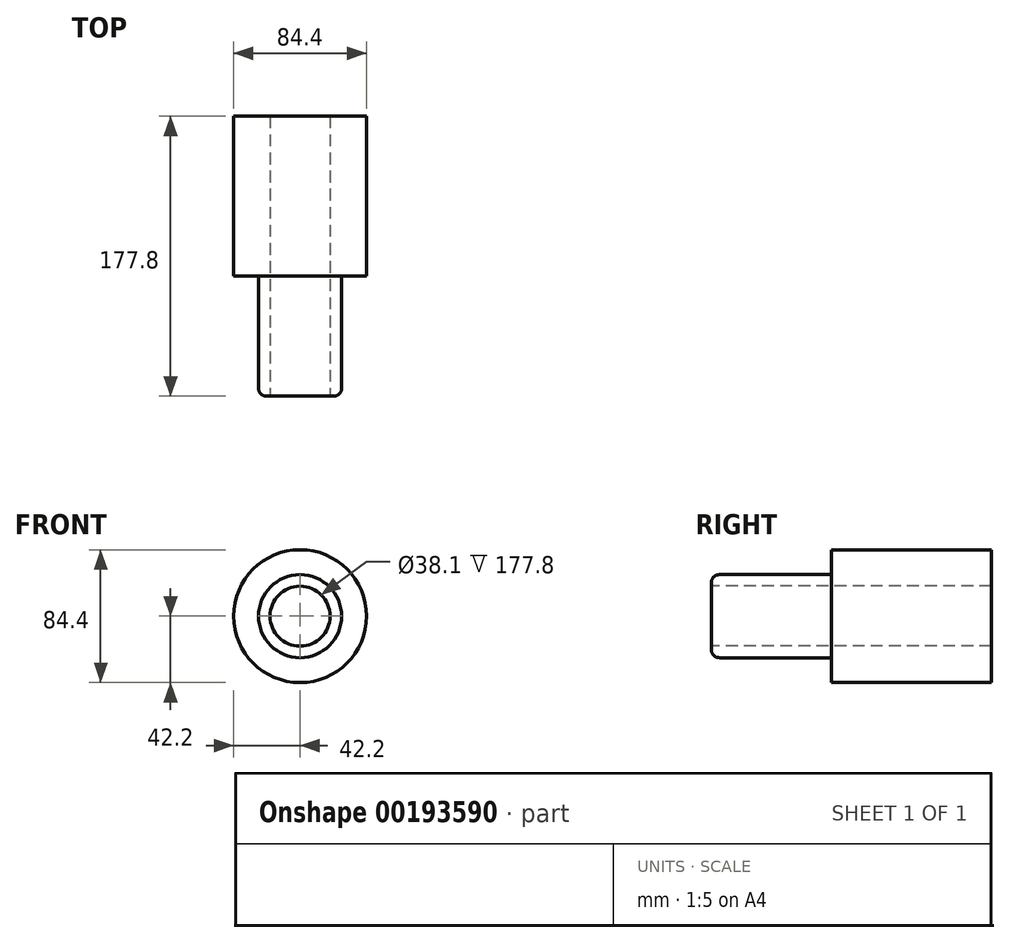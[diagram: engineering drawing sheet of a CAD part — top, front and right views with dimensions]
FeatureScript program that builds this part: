
annotation { "Feature Type Name" : "Feature", "Feature Type Description" : "" }
export const myFeature = defineFeature(function(context is Context, id is Id, definition is map)
    precondition{}
    {
        {
            var Q0;
            Q0=qCreatedBy(makeId("Front.planeOp"),FACE);
            var sketch = newSketch(context, id + "F0", { "sketchPlane" : qUnion([Q0])});
            skCircle(sketch, "E0", {"center": v(0, 0) * mm, "radius": 42.2 * mm});
            skSolve(sketch);
        }
        {
            var Q0;
            Q0=makeQuery(id+"F0.imprint","IMPRINT",FACE,{"disambiguationData":[TD([[makeQuery(id+"F0.imprint","IMPRINT",EDGE,{"derivedFrom":sQuery(id+"F0.wireOp",EDGE,"E0")}),1.0]])]});
            extrude(context, id + "F1", {"entities" : qUnion([Q0]), "depth" : 50.8 * mm});
        }
        {
            var Q0;
            Q0=qCreatedBy(makeId("Front.planeOp"),FACE);
            var sketch = newSketch(context, id + "F2", { "sketchPlane" : qUnion([Q0])});
            skCircle(sketch, "E1", {"center": v(0, 0) * mm, "radius": 26.14 * mm});
            skSolve(sketch);
        }
        {
            var Q0;
            Q0 = qSketchRegion(id + "F2", true);
            extrude(context, id + "F3", {"entities" : qUnion([Q0]), "operationType" : NewBodyOperationType.ADD, "depth" : 25.4 * mm});
        }
        {
            var Q0;
            Q0=qCreatedBy(makeId("Front.planeOp"),FACE);
            var sketch = newSketch(context, id + "F4", { "sketchPlane" : qUnion([Q0])});
            skCircle(sketch, "E2", {"center": v(0, 0) * mm, "radius": 17.71 * mm});
            skSolve(sketch);
        }
        {
            var Q0;
            Q0 = qSketchRegion(id + "F4", true);
            extrude(context, id + "F5", {"entities" : qUnion([Q0]), "operationType" : NewBodyOperationType.ADD, "depth" : 25.4 * mm});
        }
        {
            var Q0;
            Q0=qCreatedBy(makeId("Front.planeOp"),FACE);
            var sketch = newSketch(context, id + "F6", { "sketchPlane" : qUnion([Q0])});
            skCircle(sketch, "E3", {"center": v(0, 0) * mm, "radius": 23.12 * mm});
            skPoint(sketch, "E4.center.orphan", {"position": v(0, 7.38) * mm});
            skSolve(sketch);
        }
        {
            var Q0;
            Q0 = qSketchRegion(id + "F6", true);
            var Q1;
            Q1=makeQuery(id+"F1.opExtrude","CAP_FACE",FACE,{"disambiguationData":[OSD([sQuery(id+"F0.wireOp",EDGE,"E0")])],"isStart":false});
            extrude(context, id + "F7", {"entities" : qUnion([Q0, Q1]), "operationType" : NewBodyOperationType.ADD, "depth" : 50.8 * mm});
        }
        {
            var Q0;
            Q0=makeQuery(id+"F7.opExtrude","CAP_FACE",FACE,{"disambiguationData":[OSD([sQuery(id+"F0.wireOp",EDGE,"E0")])],"isStart":false});
            var sketch = newSketch(context, id + "F8", { "sketchPlane" : qUnion([Q0])});
            skCircle(sketch, "E5", {"center": v(0, 0) * mm, "radius": 26.37 * mm});
            skSolve(sketch);
        }
        {
            var Q0;
            Q0=makeQuery(id+"F8.imprint","IMPRINT",FACE,{"disambiguationData":[TD([[makeQuery(id+"F8.imprint","IMPRINT",EDGE,{"derivedFrom":sQuery(id+"F8.wireOp",EDGE,"E5")}),1.0]])]});
            extrude(context, id + "F9", {"entities" : qUnion([Q0]), "operationType" : NewBodyOperationType.ADD, "depth" : 76.2 * mm});
        }
        {
            var Q0;
            Q0=makeQuery(id+"F9.opExtrude","CAP_FACE",FACE,{"disambiguationData":[OSD([sQuery(id+"F8.wireOp",EDGE,"E5")])],"isStart":false});
            var sketch = newSketch(context, id + "F10", { "sketchPlane" : qUnion([Q0])});
            skCircle(sketch, "E6", {"center": v(0, 0) * mm, "radius": 19.05 * mm});
            skSolve(sketch);
        }
        {
            var Q0;
            Q0=makeQuery(id+"F10.imprint","IMPRINT",FACE,{"disambiguationData":[TD([[makeQuery(id+"F10.imprint","IMPRINT",EDGE,{"derivedFrom":sQuery(id+"F10.wireOp",EDGE,"E6")}),1.0]])]});
            var Q1;
            Q1=sQuery(id+"F10.wireOp",EDGE,"E6");
            extrude(context, id + "F11", {"entities" : qUnion([Q0]), "operationType" : NewBodyOperationType.REMOVE, "surfaceEntities" : qUnion([Q1]), "oppositeDirection" : true, "depth" : 254 * mm});
        }
        {
            var Q0;
            Q0=makeQuery(id+"F9.opExtrude","CAP_EDGE",EDGE,{"disambiguationData":[OSD([sQuery(id+"F8.wireOp",EDGE,"E5")])],"isStart":false});
            fillet(context, id + "F12", {"entities" : qUnion([Q0]), "radius" : 5.08 * mm, "tangentPropagation" : true, "allowEdgeOverflow" : false});
        }
    });
